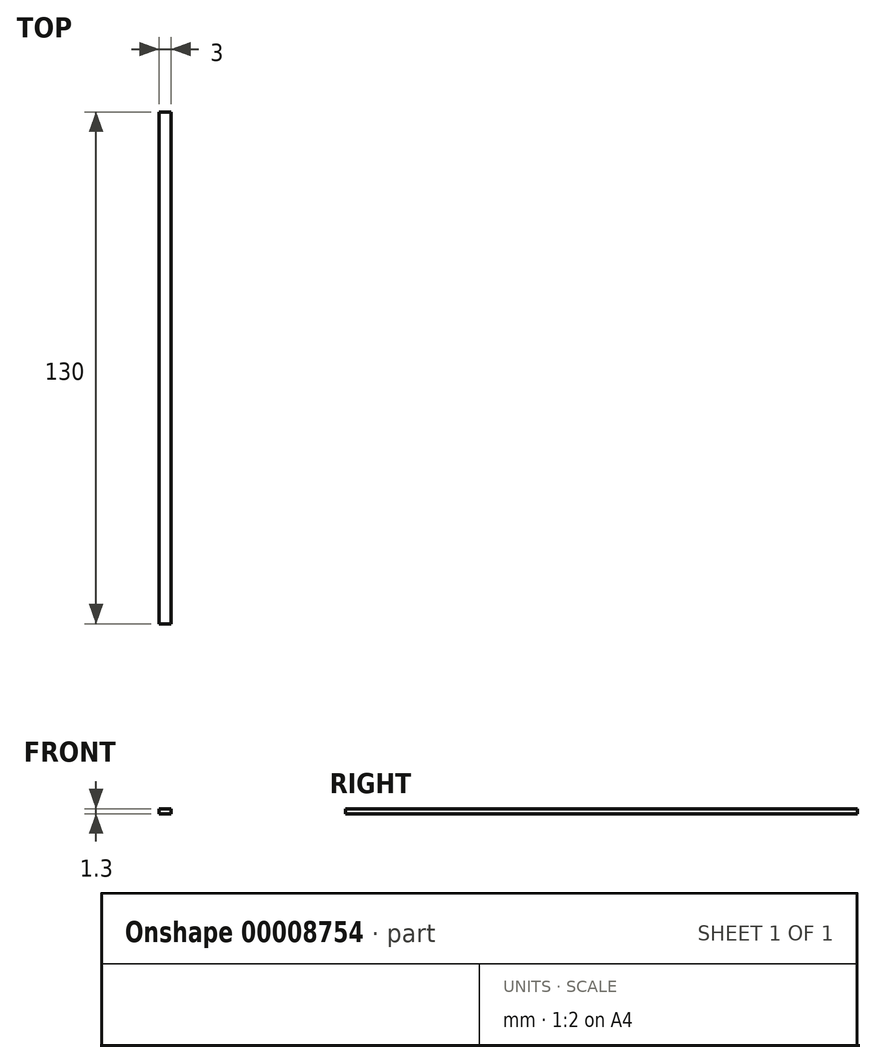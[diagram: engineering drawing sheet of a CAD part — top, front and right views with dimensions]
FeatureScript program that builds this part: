
annotation { "Feature Type Name" : "Feature", "Feature Type Description" : "" }
export const myFeature = defineFeature(function(context is Context, id is Id, definition is map)
    precondition{}
    {
        {
            var Q0;
            Q0=qCreatedBy(makeId("Front.planeOp"),FACE);
            var sketch = newSketch(context, id + "F0", { "sketchPlane" : qUnion([Q0])});
            skLineSegment(sketch, "E0.bottom", {"start": v(-3, 0) * mm, "end": v(0, 0) * mm});
            skLineSegment(sketch, "E0.top", {"start": v(-3, -1.3) * mm, "end": v(0, -1.3) * mm});
            skLineSegment(sketch, "E0.left", {"start": v(-3, 0) * mm, "end": v(-3, -1.3) * mm});
            skLineSegment(sketch, "E0.right", {"start": v(0, 0) * mm, "end": v(0, -1.3) * mm});
            skSolve(sketch);
        }
        {
            var Q0;
            Q0 = qSketchRegion(id + "F0", true);
            extrude(context, id + "F1", {"entities" : qUnion([Q0]), "depth" : 130 * mm});
        }
    });
